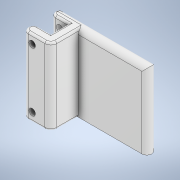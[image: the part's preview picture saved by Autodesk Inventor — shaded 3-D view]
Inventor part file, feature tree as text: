
AUTODESK INVENTOR PART (.ipt)
format: ipt  version: 2020.3 (Build 243373000, 373)  size: 202,752 bytes
history: native  units: mm
features: fillet x4, sketch x4, extrude x3, other x2, hole x1
ambient origin geometry x8: Origin, YZ Plane, XZ Plane, XY Plane, X Axis, Y Axis, Z Axis, Center Point
bodies: Body1 (feature_tree)
feature tree (14):
  other  "ソリッド1"
  extrude  "押し出し1"  Depth=5.0mm TaperAngle=0.0deg
  extrude  "押し出し2"  Depth=39.0mm
  extrude  "押し出し3"  Depth=49.0mm
  fillet  "フィレット2"  Radius=5.0mm
  other  "作業平面1"
  hole  "穴1"  [1 undecoded]
  fillet  "フィレット5"  Radius=9.0mm
  fillet  "フィレット6"  Radius=9.0mm
  fillet  "フィレット7"  Radius=5.0mm
  sketch  "スケッチ1"
  sketch  "スケッチ2"
  sketch  "スケッチ3"
  sketch  "スケッチ6"
note: 1 required parameter value undecoded (feature->parameter linkage not recoverable at this tier; creation-order binding heuristic only, values carry confidence <= 0.55)
